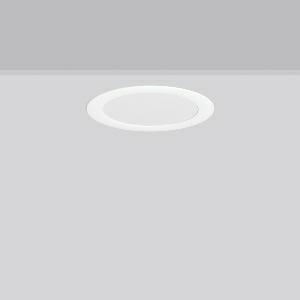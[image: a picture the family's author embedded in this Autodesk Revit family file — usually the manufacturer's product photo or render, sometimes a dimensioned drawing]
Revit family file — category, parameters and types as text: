
# Revit family: toledo_flat_round_672224_002_6616
name_source: partatom
category: Lighting Fixtures
units: mm (PartAtom-declared; Revit-internal decimal feet)

## family parameters
Cut with Voids When Loaded = No
Host = Face
Light Source = No
Part Type = Normal
Room Calculation Point = No
Round Connector Dimension = Use Diameter
Shared = No

## types (1)
- TOLEDO FLAT round (1 x LED Modul 830, 1650 lm, 3000)
    Apparent Load = 17 VA
    CIE Flux Codes = 48 79 96 100 100
    Color Rendering = 80
    Color Temperature = 3000
    Default Elevation = 1800 mm
    Description = Series: TOLEDO FLAT round
Ultra thin recessed downlight. For escape route illumination. Housing: die-cast aluminium, powder-coated. Lightguide and diffuser made of non-yellowing plastic (PMMA). Diffuser opal matt plastic. Ceiling installation with spring system. Including separate LED converter with connecting cable 250 mm. Self-contained system with automatic self-test. External driver with simple plug-in locking system. 
Colour: white
Diameter: 255 mm
Height: 3 mm
Cut-out diameter: 234 mm
Recess height: 100 mm
Luminaire: recess height: 60-80 mm
Weight: 1.76 kg
Operating mode: maintained power mode
Duration time: 3 h
Lamp: LED
Socket: without socket
Colour temperature: 3000K
Colour rendering index (CRI): 80
System power: 17 W
Rated luminous flux: 1650 lm
Luminous flux, emergency: 450 lm
System power, emergency: -
Control gear: Regulated power supply
Protection class: I
Type of protection: IP 54
    Height = 0 mm  [stored 0 ft]
    Lamp = 1 x LED Modul 830
    Lamp Light Flux = 1650 lm
    Lamp count = 1
    Length = 255 mm
    Lifetime = 50000 h
    Luminous efficacy = 97 lm/W
    Manufacturer = RZB
    ModVariant = No
    Model = 672224.002
    Mounting Place = Ceiling
    Mounting Type = Recessed
    Number of Poles = 1
    OnlyDefault = Yes
    Power Factor = 1
    Product Name = TOLEDO FLAT round
    Product group = Recessed downlights
    ProductGroupID = 402
    Protection Class = Protection class I
    Protection Degree = Degree of protection
    RLX_Detail_Level = 1
    RLX_Emergency_Light_Flux = 450 lm
    RLX_Emergency_Type = 3
    RLX_Emergency_Type_DB = Yes
    RlxData = <blob elided: 31089 chars, md5=8d6d5bae>
    Socket = socket
    Standby Power = 0 W
    System Light Flux = 1650 lm
    System Power = 17 W
    Type Comments = Product without accessories
    Type Image = 901453.002.jpg
    URL = http://relux.com
    VarID = ---
    Voltage = 0 V
    Weight = 0.00 kg
    Width = 0 mm  [stored 0 ft]

note: [stored X ft] marks values corroborated as IEEE doubles in the binary element streams (Revit-internal decimal feet)

## geometry (parser evidence)
native form markers: Blend x4, Sweep x11
no freeform markers — native parametric forms only
